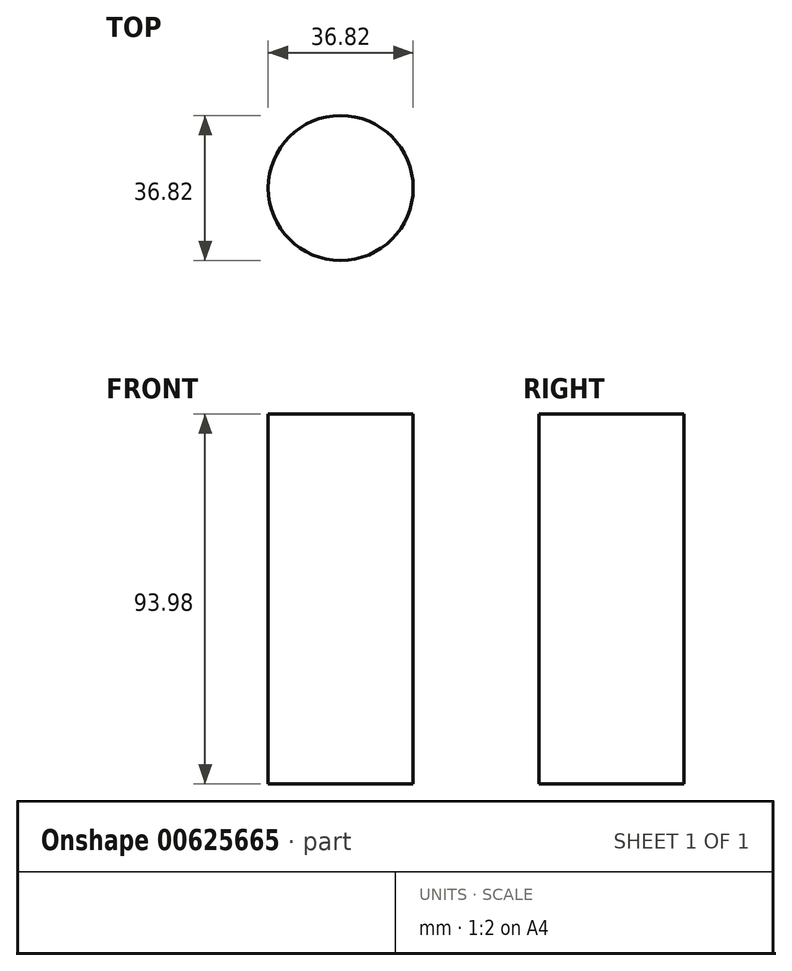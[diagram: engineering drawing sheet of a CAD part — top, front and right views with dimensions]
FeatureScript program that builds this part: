
annotation { "Feature Type Name" : "Feature", "Feature Type Description" : "" }
export const myFeature = defineFeature(function(context is Context, id is Id, definition is map)
    precondition{}
    {
        {
            var Q0;
            Q0=qCreatedBy(makeId("Top.planeOp"),FACE);
            var sketch = newSketch(context, id + "F0", { "sketchPlane" : qUnion([Q0])});
            skCircle(sketch, "E0", {"center": v(0, 0) * mm, "radius": 18.41 * mm});
            skSolve(sketch);
        }
        {
            var Q0;
            Q0=makeQuery(id+"F0.imprint","IMPRINT",FACE,{"disambiguationData":[TD([[makeQuery(id+"F0.imprint","IMPRINT",EDGE,{"derivedFrom":sQuery(id+"F0.wireOp",EDGE,"E0")}),1.0]])]});
            extrude(context, id + "F1", {"entities" : qUnion([Q0]), "depth" : 93.98 * mm, "offsetDistance" : 25.4 * mm});
        }
    });
